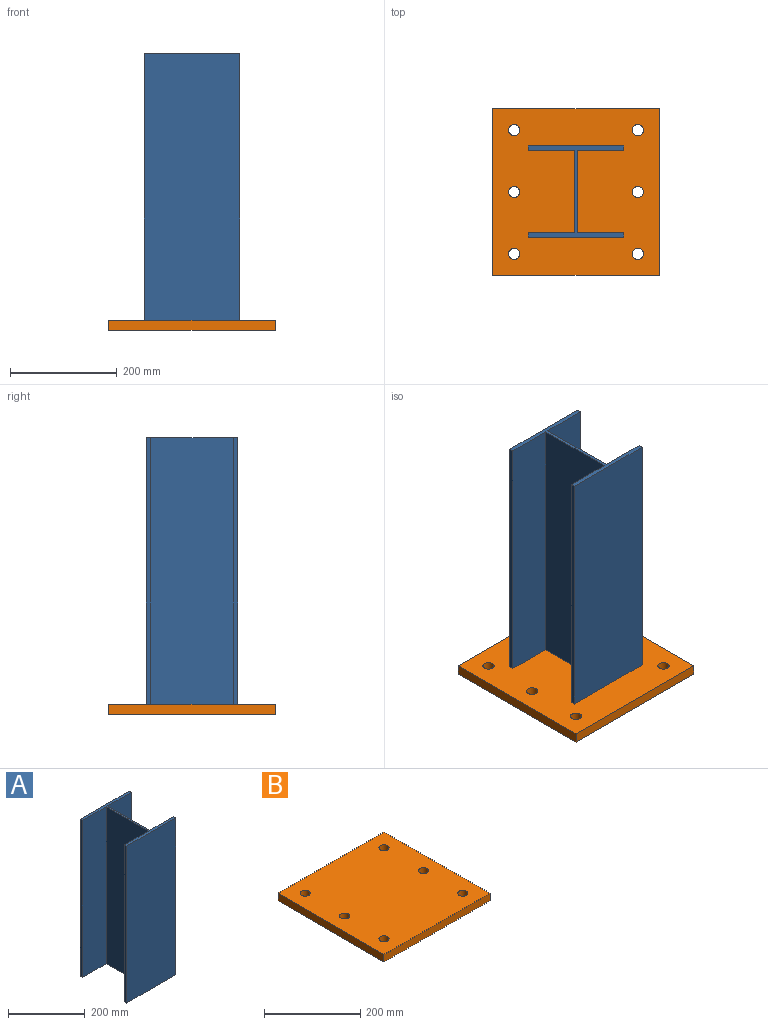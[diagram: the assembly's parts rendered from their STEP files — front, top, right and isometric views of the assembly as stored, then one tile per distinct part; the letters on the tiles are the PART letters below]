
ASSEMBLY  parts=2 mates=1
PART A: 14 faces, bbox 180x171x500 mm
  f0: plane 500x180mm, normal (0,-1,0), area 90000mm2, adj f1,f11,f12,f13
  f1: plane 500x8mm, normal (1,0,0), area 4000mm2, adj f0,f2,f12,f13
  f2: plane 500x87.35mm, normal (0,1,0), area 43675mm2, adj f1,f3,f12,f13
  f3: plane 500x155mm, normal (1,0,0), area 77500mm2, adj f2,f4,f12,f13
  f4: plane 500x87.35mm, normal (0,-1,0), area 43675mm2, adj f3,f5,f12,f13
  f5: plane 500x8mm, normal (1,0,0), area 4000mm2, adj f4,f6,f12,f13
  f6: plane 500x180mm, normal (0,1,0), area 90000mm2, adj f5,f7,f12,f13
  f7: plane 500x8mm, normal (-1,0,0), area 4000mm2, adj f6,f8,f12,f13
  f8: plane 500x87.35mm, normal (0,-1,0), area 43675mm2, adj f7,f9,f12,f13
  f9: plane 500x155mm, normal (-1,0,0), area 77500mm2, adj f8,f10,f12,f13
  f10: plane 500x87.35mm, normal (0,1,0), area 43675mm2, adj f9,f11,f12,f13
  f11: plane 500x8mm, normal (-1,0,0), area 4000mm2, adj f0,f10,f12,f13
  f12: plane 180x171mm, normal (0,0,1), area 3701.5mm2, adj f0,f1,f2,f3,f4,f5,f6,f7
  f13: plane 180x171mm, normal (0,0,-1), area 3701.5mm2, adj f0,f1,f2,f3,f4,f5,f6,f7
PART B: 12 faces, bbox 312x312x19 mm
  f0: plane 312x19mm, normal (1,0,0), area 5928mm2, adj f1,f3,f4,f5
  f1: plane 312x19mm, normal (0,1,0), area 5928mm2, adj f0,f2,f4,f5
  f2: plane 312x19mm, normal (-1,0,0), area 5928mm2, adj f1,f3,f4,f5
  f3: plane 312x19mm, normal (0,-1,0), area 5928mm2, adj f0,f2,f4,f5
  f4: plane 312x312mm, normal (0,0,1), area 95265.8mm2, adj f0,f1,f2,f3,f6,f7,f8,f9
  f5: plane 312x312mm, normal (0,0,-1), area 95265.8mm2, adj f0,f1,f2,f3,f6,f7,f8,f9
  f6: cylinder r=10.5mm len=21mm, axis (0,0,-1), area 1253.5mm2, adj f4,f5
  f7: cylinder r=10.5mm len=21mm, axis (0,0,-1), area 1253.5mm2, adj f4,f5
  f8: cylinder r=10.5mm len=21mm, axis (0,0,-1), area 1253.5mm2, adj f4,f5
  f9: cylinder r=10.5mm len=21mm, axis (0,0,-1), area 1253.5mm2, adj f4,f5
  f10: cylinder r=10.5mm len=21mm, axis (0,0,-1), area 1253.5mm2, adj f4,f5
  f11: cylinder r=10.5mm len=21mm, axis (0,0,-1), area 1253.5mm2, adj f4,f5
PLACE A t=(-44.46,-58.64,27.36)mm
PLACE B t=(-39.62,-10.97,8.36)mm fixed
MATE fastened B.f4 <-> A.f13  axis (0,0,1) through (-39.62,-10.97,27.36)mm
